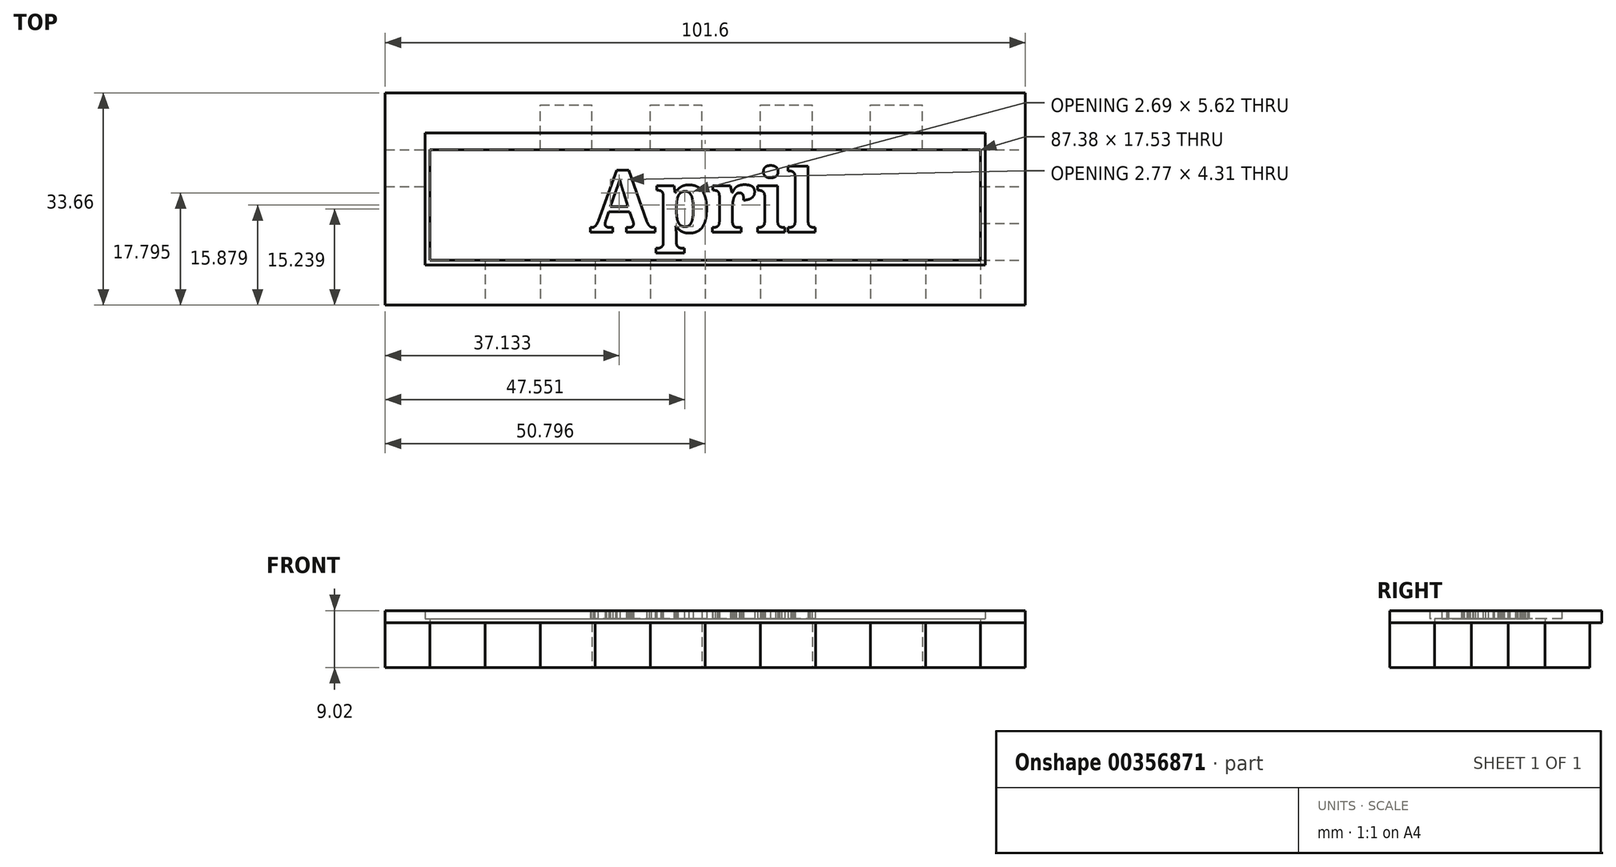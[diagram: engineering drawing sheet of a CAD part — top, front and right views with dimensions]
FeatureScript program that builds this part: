
annotation { "Feature Type Name" : "Feature", "Feature Type Description" : "" }
export const myFeature = defineFeature(function(context is Context, id is Id, definition is map)
    precondition{}
    {
        {
            var Q0;
            Q0=qCreatedBy(makeId("Top.planeOp"),FACE);
            var sketch = newSketch(context, id + "F0", { "sketchPlane" : qUnion([Q0])});
            skLineSegment(sketch, "E0.bottom", {"start": v(-52.12, 11.37) * mm, "end": v(49.48, 11.37) * mm});
            skLineSegment(sketch, "E0.top", {"start": v(-52.12, -20.38) * mm, "end": v(49.48, -20.38) * mm});
            skLineSegment(sketch, "E0.left", {"start": v(-52.12, 11.37) * mm, "end": v(-52.12, -20.38) * mm});
            skLineSegment(sketch, "E0.right", {"start": v(49.48, 11.37) * mm, "end": v(49.48, -20.38) * mm});
            skLineSegment(sketch, "E1.bottom", {"start": v(-52.12, 11.37) * mm, "end": v(-45.01, 11.37) * mm});
            skLineSegment(sketch, "E1.top", {"start": v(-52.12, 4.26) * mm, "end": v(-45.01, 4.26) * mm});
            skLineSegment(sketch, "E1.left", {"start": v(-52.12, 11.37) * mm, "end": v(-52.12, 4.26) * mm});
            skLineSegment(sketch, "E1.right", {"start": v(-45.01, 11.37) * mm, "end": v(-45.01, 4.26) * mm});
            skLineSegment(sketch, "E2.bottom", {"start": v(-45.01, 11.37) * mm, "end": v(-36.78, 11.37) * mm});
            skLineSegment(sketch, "E2.top", {"start": v(-45.01, 4.26) * mm, "end": v(-36.78, 4.26) * mm});
            skLineSegment(sketch, "E2.right", {"start": v(-36.78, 11.37) * mm, "end": v(-36.78, 4.26) * mm});
            skLineSegment(sketch, "E3.bottom", {"start": v(-36.78, 4.26) * mm, "end": v(-27.54, 4.26) * mm});
            skLineSegment(sketch, "E3.top", {"start": v(-36.78, 11.37) * mm, "end": v(-27.54, 11.37) * mm});
            skLineSegment(sketch, "E3.left", {"start": v(-36.78, 4.26) * mm, "end": v(-36.78, 11.37) * mm});
            skLineSegment(sketch, "E3.right", {"start": v(-27.54, 4.26) * mm, "end": v(-27.54, 11.37) * mm});
            skLineSegment(sketch, "E4.bottom", {"start": v(-27.54, 4.26) * mm, "end": v(-19.3, 4.26) * mm});
            skLineSegment(sketch, "E4.top", {"start": v(-27.54, 11.37) * mm, "end": v(-19.3, 11.37) * mm});
            skLineSegment(sketch, "E4.right", {"start": v(-19.3, 4.26) * mm, "end": v(-19.3, 11.37) * mm});
            skLineSegment(sketch, "E5.bottom", {"start": v(-19.3, 4.26) * mm, "end": v(-10.06, 4.26) * mm});
            skLineSegment(sketch, "E5.top", {"start": v(-19.3, 11.37) * mm, "end": v(-10.06, 11.37) * mm});
            skLineSegment(sketch, "E5.right", {"start": v(-10.06, 4.26) * mm, "end": v(-10.06, 11.37) * mm});
            skLineSegment(sketch, "E6.bottom", {"start": v(-10.06, 4.26) * mm, "end": v(-10.06, 4.26) * mm});
            skLineSegment(sketch, "E6.top", {"start": v(-10.06, 11.37) * mm, "end": v(-10.06, 11.37) * mm});
            skLineSegment(sketch, "E7.bottom", {"start": v(-10.06, 4.26) * mm, "end": v(-1.83, 4.26) * mm});
            skLineSegment(sketch, "E7.top", {"start": v(-10.06, 11.37) * mm, "end": v(-1.83, 11.37) * mm});
            skLineSegment(sketch, "E7.right", {"start": v(-1.83, 4.26) * mm, "end": v(-1.83, 11.37) * mm});
            skLineSegment(sketch, "E8.bottom", {"start": v(-1.83, 4.26) * mm, "end": v(7.41, 4.26) * mm});
            skLineSegment(sketch, "E8.top", {"start": v(-1.83, 11.37) * mm, "end": v(7.41, 11.37) * mm});
            skLineSegment(sketch, "E8.right", {"start": v(7.41, 4.26) * mm, "end": v(7.41, 11.37) * mm});
            skLineSegment(sketch, "E9.bottom", {"start": v(7.41, 4.26) * mm, "end": v(15.64, 4.26) * mm});
            skLineSegment(sketch, "E9.top", {"start": v(7.41, 11.37) * mm, "end": v(15.64, 11.37) * mm});
            skLineSegment(sketch, "E9.right", {"start": v(15.64, 4.26) * mm, "end": v(15.64, 11.37) * mm});
            skLineSegment(sketch, "E10.bottom", {"start": v(15.64, 4.26) * mm, "end": v(24.89, 4.26) * mm});
            skLineSegment(sketch, "E10.top", {"start": v(15.64, 11.37) * mm, "end": v(24.89, 11.37) * mm});
            skLineSegment(sketch, "E10.right", {"start": v(24.89, 4.26) * mm, "end": v(24.89, 11.37) * mm});
            skLineSegment(sketch, "E11.bottom", {"start": v(24.89, 4.26) * mm, "end": v(24.89, 4.26) * mm});
            skLineSegment(sketch, "E11.top", {"start": v(24.89, 11.37) * mm, "end": v(24.89, 11.37) * mm});
            skLineSegment(sketch, "E12.bottom", {"start": v(24.89, 4.26) * mm, "end": v(33.12, 4.26) * mm});
            skLineSegment(sketch, "E12.top", {"start": v(24.89, 11.37) * mm, "end": v(33.12, 11.37) * mm});
            skLineSegment(sketch, "E12.right", {"start": v(33.12, 4.26) * mm, "end": v(33.12, 11.37) * mm});
            skLineSegment(sketch, "E13.bottom", {"start": v(33.12, 4.26) * mm, "end": v(42.36, 4.26) * mm});
            skLineSegment(sketch, "E13.top", {"start": v(33.12, 11.37) * mm, "end": v(42.36, 11.37) * mm});
            skLineSegment(sketch, "E13.right", {"start": v(42.36, 4.26) * mm, "end": v(42.36, 11.37) * mm});
            skLineSegment(sketch, "E14.bottom", {"start": v(42.36, 4.26) * mm, "end": v(49.48, 4.26) * mm});
            skLineSegment(sketch, "E14.top", {"start": v(42.36, 11.37) * mm, "end": v(49.48, 11.37) * mm});
            skLineSegment(sketch, "E14.right", {"start": v(49.48, 4.26) * mm, "end": v(49.48, 11.37) * mm});
            skLineSegment(sketch, "E15.bottom", {"start": v(-52.12, -20.38) * mm, "end": v(-45.01, -20.38) * mm});
            skLineSegment(sketch, "E15.top", {"start": v(-52.12, -13.26) * mm, "end": v(-45.01, -13.26) * mm});
            skLineSegment(sketch, "E15.left", {"start": v(-52.12, -20.38) * mm, "end": v(-52.12, -13.26) * mm});
            skLineSegment(sketch, "E15.right", {"start": v(-45.01, -20.38) * mm, "end": v(-45.01, -13.26) * mm});
            skLineSegment(sketch, "E16.bottom", {"start": v(-45.01, -13.26) * mm, "end": v(-45.01, -13.26) * mm});
            skLineSegment(sketch, "E16.top", {"start": v(-45.01, -20.38) * mm, "end": v(-45.01, -20.38) * mm});
            skLineSegment(sketch, "E16.left", {"start": v(-45.01, -13.26) * mm, "end": v(-45.01, -20.38) * mm});
            skLineSegment(sketch, "E16.right", {"start": v(-45.01, -13.26) * mm, "end": v(-45.01, -20.38) * mm});
            skLineSegment(sketch, "E17.bottom", {"start": v(-45.01, -13.26) * mm, "end": v(-36.27, -13.26) * mm});
            skLineSegment(sketch, "E17.top", {"start": v(-45.01, -20.38) * mm, "end": v(-36.27, -20.38) * mm});
            skLineSegment(sketch, "E17.right", {"start": v(-36.27, -13.26) * mm, "end": v(-36.27, -20.38) * mm});
            skLineSegment(sketch, "E18.bottom", {"start": v(-36.27, -13.26) * mm, "end": v(-36.27, -13.26) * mm});
            skLineSegment(sketch, "E18.top", {"start": v(-36.27, -20.38) * mm, "end": v(-36.27, -20.38) * mm});
            skLineSegment(sketch, "E19.bottom", {"start": v(-36.27, -13.26) * mm, "end": v(-27.54, -13.26) * mm});
            skLineSegment(sketch, "E19.top", {"start": v(-36.27, -20.38) * mm, "end": v(-27.54, -20.38) * mm});
            skLineSegment(sketch, "E19.right", {"start": v(-27.54, -13.26) * mm, "end": v(-27.54, -20.38) * mm});
            skLineSegment(sketch, "E20.bottom", {"start": v(-27.54, -13.26) * mm, "end": v(-18.8, -13.26) * mm});
            skLineSegment(sketch, "E20.top", {"start": v(-27.54, -20.38) * mm, "end": v(-18.8, -20.38) * mm});
            skLineSegment(sketch, "E20.right", {"start": v(-18.8, -13.26) * mm, "end": v(-18.8, -20.38) * mm});
            skLineSegment(sketch, "E21.bottom", {"start": v(-18.8, -13.26) * mm, "end": v(-10.06, -13.26) * mm});
            skLineSegment(sketch, "E21.top", {"start": v(-18.8, -20.38) * mm, "end": v(-10.06, -20.38) * mm});
            skLineSegment(sketch, "E21.right", {"start": v(-10.06, -13.26) * mm, "end": v(-10.06, -20.38) * mm});
            skLineSegment(sketch, "E22.bottom", {"start": v(-10.06, -13.26) * mm, "end": v(-1.32, -13.26) * mm});
            skLineSegment(sketch, "E22.top", {"start": v(-10.06, -20.38) * mm, "end": v(-1.32, -20.38) * mm});
            skLineSegment(sketch, "E22.right", {"start": v(-1.32, -13.26) * mm, "end": v(-1.32, -20.38) * mm});
            skLineSegment(sketch, "E23.bottom", {"start": v(-1.32, -13.26) * mm, "end": v(7.41, -13.26) * mm});
            skLineSegment(sketch, "E23.top", {"start": v(-1.32, -20.38) * mm, "end": v(7.41, -20.38) * mm});
            skLineSegment(sketch, "E23.right", {"start": v(7.41, -13.26) * mm, "end": v(7.41, -20.38) * mm});
            skLineSegment(sketch, "E24.bottom", {"start": v(7.41, -13.26) * mm, "end": v(16.15, -13.26) * mm});
            skLineSegment(sketch, "E24.top", {"start": v(7.41, -20.38) * mm, "end": v(16.15, -20.38) * mm});
            skLineSegment(sketch, "E24.right", {"start": v(16.15, -13.26) * mm, "end": v(16.15, -20.38) * mm});
            skLineSegment(sketch, "E25.bottom", {"start": v(16.15, -13.26) * mm, "end": v(24.89, -13.26) * mm});
            skLineSegment(sketch, "E25.top", {"start": v(16.15, -20.38) * mm, "end": v(24.89, -20.38) * mm});
            skLineSegment(sketch, "E25.right", {"start": v(24.89, -13.26) * mm, "end": v(24.89, -20.38) * mm});
            skLineSegment(sketch, "E26.bottom", {"start": v(24.89, -13.26) * mm, "end": v(33.63, -13.26) * mm});
            skLineSegment(sketch, "E26.top", {"start": v(24.89, -20.38) * mm, "end": v(33.63, -20.38) * mm});
            skLineSegment(sketch, "E26.right", {"start": v(33.63, -13.26) * mm, "end": v(33.63, -20.38) * mm});
            skLineSegment(sketch, "E27.bottom", {"start": v(33.63, -13.26) * mm, "end": v(42.36, -13.26) * mm});
            skLineSegment(sketch, "E27.top", {"start": v(33.63, -20.38) * mm, "end": v(42.36, -20.38) * mm});
            skLineSegment(sketch, "E27.right", {"start": v(42.36, -13.26) * mm, "end": v(42.36, -20.38) * mm});
            skLineSegment(sketch, "E28.bottom", {"start": v(42.36, -13.26) * mm, "end": v(49.48, -13.26) * mm});
            skLineSegment(sketch, "E28.top", {"start": v(42.36, -20.38) * mm, "end": v(49.48, -20.38) * mm});
            skLineSegment(sketch, "E28.right", {"start": v(49.48, -13.26) * mm, "end": v(49.48, -20.38) * mm});
            skLineSegment(sketch, "E29.top", {"start": v(-52.12, -1.58) * mm, "end": v(-45.01, -1.58) * mm});
            skLineSegment(sketch, "E29.left", {"start": v(-52.12, 4.26) * mm, "end": v(-52.12, -1.58) * mm});
            skLineSegment(sketch, "E29.right", {"start": v(-45.01, 4.26) * mm, "end": v(-45.01, -1.58) * mm});
            skLineSegment(sketch, "E30.top", {"start": v(-52.12, -7.42) * mm, "end": v(-45.01, -7.42) * mm});
            skLineSegment(sketch, "E30.left", {"start": v(-52.12, -1.58) * mm, "end": v(-52.12, -7.42) * mm});
            skLineSegment(sketch, "E30.right", {"start": v(-45.01, -1.58) * mm, "end": v(-45.01, -7.42) * mm});
            skLineSegment(sketch, "E31.bottom", {"start": v(-45.01, -7.42) * mm, "end": v(-52.12, -7.42) * mm});
            skLineSegment(sketch, "E31.top", {"start": v(-45.01, -13.26) * mm, "end": v(-52.12, -13.26) * mm});
            skLineSegment(sketch, "E31.left", {"start": v(-45.01, -7.42) * mm, "end": v(-45.01, -13.26) * mm});
            skLineSegment(sketch, "E31.right", {"start": v(-52.12, -7.42) * mm, "end": v(-52.12, -13.26) * mm});
            skLineSegment(sketch, "E32.top", {"start": v(42.36, -1.58) * mm, "end": v(49.48, -1.58) * mm});
            skLineSegment(sketch, "E32.left", {"start": v(42.36, 4.26) * mm, "end": v(42.36, -1.58) * mm});
            skLineSegment(sketch, "E32.right", {"start": v(49.48, 4.26) * mm, "end": v(49.48, -1.58) * mm});
            skLineSegment(sketch, "E33.top", {"start": v(42.36, -7.42) * mm, "end": v(49.48, -7.42) * mm});
            skLineSegment(sketch, "E33.left", {"start": v(42.36, -1.58) * mm, "end": v(42.36, -7.42) * mm});
            skLineSegment(sketch, "E33.right", {"start": v(49.48, -1.58) * mm, "end": v(49.48, -7.42) * mm});
            skLineSegment(sketch, "E34.left", {"start": v(42.36, -7.42) * mm, "end": v(42.36, -13.26) * mm});
            skLineSegment(sketch, "E34.right", {"start": v(49.48, -7.42) * mm, "end": v(49.48, -13.26) * mm});
            skSolve(sketch);
        }
        {
            var Q0;
            Q0=makeQuery(id+"F0.imprint","IMPRINT",FACE,{"disambiguationData":[TD([[makeQuery(id+"F0.imprint","IMPRINT",EDGE,{"derivedFrom":sQuery(id+"F0.wireOp",EDGE,"E2.top")}),-1.0]])]});
            var Q1;
            Q1=makeQuery(id+"F0.imprint","IMPRINT",FACE,{"disambiguationData":[TD([[makeQuery(id+"F0.imprint","IMPRINT",EDGE,{"derivedFrom":sQuery(id+"F0.wireOp",EDGE,"E2.bottom")}),-1.0]])]});
            var Q2;
            Q2=makeQuery(id+"F0.imprint","IMPRINT",FACE,{"disambiguationData":[TD([[makeQuery(id+"F0.imprint","IMPRINT",EDGE,{"derivedFrom":sQuery(id+"F0.wireOp",EDGE,"E4.bottom")}),1.0]])]});
            var Q3;
            Q3=makeQuery(id+"F0.imprint","IMPRINT",FACE,{"disambiguationData":[TD([[makeQuery(id+"F0.imprint","IMPRINT",EDGE,{"derivedFrom":sQuery(id+"F0.wireOp",EDGE,"E7.bottom")}),1.0]])]});
            var Q4;
            Q4=makeQuery(id+"F0.imprint","IMPRINT",FACE,{"disambiguationData":[TD([[makeQuery(id+"F0.imprint","IMPRINT",EDGE,{"derivedFrom":sQuery(id+"F0.wireOp",EDGE,"E9.bottom")}),1.0]])]});
            var Q5;
            Q5=makeQuery(id+"F0.imprint","IMPRINT",FACE,{"disambiguationData":[TD([[makeQuery(id+"F0.imprint","IMPRINT",EDGE,{"derivedFrom":sQuery(id+"F0.wireOp",EDGE,"E12.bottom")}),1.0]])]});
            var Q6;
            Q6=makeQuery(id+"F0.imprint","IMPRINT",FACE,{"disambiguationData":[TD([[makeQuery(id+"F0.imprint","IMPRINT",EDGE,{"derivedFrom":sQuery(id+"F0.wireOp",EDGE,"E14.bottom")}),-1.0]])]});
            var Q7;
            Q7=makeQuery(id+"F0.imprint","IMPRINT",FACE,{"disambiguationData":[TD([[makeQuery(id+"F0.imprint","IMPRINT",EDGE,{"derivedFrom":sQuery(id+"F0.wireOp",EDGE,"E33.top")}),-1.0]])]});
            var Q8;
            Q8=makeQuery(id+"F0.imprint","IMPRINT",FACE,{"disambiguationData":[TD([[makeQuery(id+"F0.imprint","IMPRINT",EDGE,{"derivedFrom":sQuery(id+"F0.wireOp",EDGE,"E27.bottom")}),-1.0]])]});
            var Q9;
            Q9=makeQuery(id+"F0.imprint","IMPRINT",FACE,{"disambiguationData":[TD([[makeQuery(id+"F0.imprint","IMPRINT",EDGE,{"derivedFrom":sQuery(id+"F0.wireOp",EDGE,"E25.bottom")}),-1.0]])]});
            var Q10;
            Q10=makeQuery(id+"F0.imprint","IMPRINT",FACE,{"disambiguationData":[TD([[makeQuery(id+"F0.imprint","IMPRINT",EDGE,{"derivedFrom":sQuery(id+"F0.wireOp",EDGE,"E23.bottom")}),-1.0]])]});
            var Q11;
            Q11=makeQuery(id+"F0.imprint","IMPRINT",FACE,{"disambiguationData":[TD([[makeQuery(id+"F0.imprint","IMPRINT",EDGE,{"derivedFrom":sQuery(id+"F0.wireOp",EDGE,"E21.bottom")}),-1.0]])]});
            var Q12;
            Q12=makeQuery(id+"F0.imprint","IMPRINT",FACE,{"disambiguationData":[TD([[makeQuery(id+"F0.imprint","IMPRINT",EDGE,{"derivedFrom":sQuery(id+"F0.wireOp",EDGE,"E19.bottom")}),-1.0]])]});
            var Q13;
            Q13=makeQuery(id+"F0.imprint","IMPRINT",FACE,{"disambiguationData":[TD([[makeQuery(id+"F0.imprint","IMPRINT",EDGE,{"derivedFrom":sQuery(id+"F0.wireOp",EDGE,"E31.bottom")}),1.0]])]});
            var Q14;
            Q14=makeQuery(id+"F0.imprint","IMPRINT",FACE,{"disambiguationData":[TD([[makeQuery(id+"F0.imprint","IMPRINT",EDGE,{"derivedFrom":sQuery(id+"F0.wireOp",EDGE,"E1.top")}),-1.0]])]});
            extrude(context, id + "F1", {"entities" : qUnion([Q0, Q1, Q2, Q3, Q4, Q5, Q6, Q7, Q8, Q9, Q10, Q11, Q12, Q13, Q14]), "depth" : 7.11 * mm});
        }
        {
            var Q0;
            Q0=makeQuery(id+"F1.opExtrude","CAP_FACE",FACE,{"disambiguationData":[OSD([sQuery(id+"F0.wireOp",EDGE,"E2.bottom"),sQuery(id+"F0.wireOp",EDGE,"E1.right"),sQuery(id+"F0.wireOp",EDGE,"E3.bottom"),sQuery(id+"F0.wireOp",EDGE,"E3.left"),sQuery(id+"F0.wireOp",EDGE,"E4.top"),sQuery(id+"F0.wireOp",EDGE,"E3.right"),sQuery(id+"F0.wireOp",EDGE,"E5.bottom"),sQuery(id+"F0.wireOp",EDGE,"E4.right"),sQuery(id+"F0.wireOp",EDGE,"E6.top"),sQuery(id+"F0.wireOp",EDGE,"E5.right"),sQuery(id+"F0.wireOp",EDGE,"E7.bottom"),sQuery(id+"F0.wireOp",EDGE,"E5.right"),sQuery(id+"F0.wireOp",EDGE,"E8.top"),sQuery(id+"F0.wireOp",EDGE,"E7.right"),sQuery(id+"F0.wireOp",EDGE,"E9.bottom"),sQuery(id+"F0.wireOp",EDGE,"E8.right"),sQuery(id+"F0.wireOp",EDGE,"E10.top"),sQuery(id+"F0.wireOp",EDGE,"E9.right"),sQuery(id+"F0.wireOp",EDGE,"E11.bottom"),sQuery(id+"F0.wireOp",EDGE,"E10.right"),sQuery(id+"F0.wireOp",EDGE,"E12.top"),sQuery(id+"F0.wireOp",EDGE,"E10.right"),sQuery(id+"F0.wireOp",EDGE,"E13.bottom"),sQuery(id+"F0.wireOp",EDGE,"E12.right"),sQuery(id+"F0.wireOp",EDGE,"E16.bottom"),sQuery(id+"F0.wireOp",EDGE,"E17.top"),sQuery(id+"F0.wireOp",EDGE,"E16.left"),sQuery(id+"F0.wireOp",EDGE,"E18.bottom"),sQuery(id+"F0.wireOp",EDGE,"E17.right"),sQuery(id+"F0.wireOp",EDGE,"E19.top"),sQuery(id+"F0.wireOp",EDGE,"E17.right"),sQuery(id+"F0.wireOp",EDGE,"E20.bottom"),sQuery(id+"F0.wireOp",EDGE,"E19.right"),sQuery(id+"F0.wireOp",EDGE,"E21.top"),sQuery(id+"F0.wireOp",EDGE,"E20.right"),sQuery(id+"F0.wireOp",EDGE,"E22.bottom"),sQuery(id+"F0.wireOp",EDGE,"E21.right"),sQuery(id+"F0.wireOp",EDGE,"E23.top"),sQuery(id+"F0.wireOp",EDGE,"E22.right"),sQuery(id+"F0.wireOp",EDGE,"E24.bottom"),sQuery(id+"F0.wireOp",EDGE,"E23.right"),sQuery(id+"F0.wireOp",EDGE,"E25.top"),sQuery(id+"F0.wireOp",EDGE,"E24.right"),sQuery(id+"F0.wireOp",EDGE,"E26.bottom"),sQuery(id+"F0.wireOp",EDGE,"E25.right"),sQuery(id+"F0.wireOp",EDGE,"E27.top"),sQuery(id+"F0.wireOp",EDGE,"E26.right"),sQuery(id+"F0.wireOp",EDGE,"E27.right"),sQuery(id+"F0.wireOp",EDGE,"E1.top"),sQuery(id+"F0.wireOp",EDGE,"E29.left"),sQuery(id+"F0.wireOp",EDGE,"E29.top"),sQuery(id+"F0.wireOp",EDGE,"E30.right"),sQuery(id+"F0.wireOp",EDGE,"E31.bottom"),sQuery(id+"F0.wireOp",EDGE,"E31.top"),sQuery(id+"F0.wireOp",EDGE,"E31.right"),sQuery(id+"F0.wireOp",EDGE,"E14.bottom"),sQuery(id+"F0.wireOp",EDGE,"E32.right"),sQuery(id+"F0.wireOp",EDGE,"E32.top"),sQuery(id+"F0.wireOp",EDGE,"E33.left"),sQuery(id+"F0.wireOp",EDGE,"E33.top"),sQuery(id+"F0.wireOp",EDGE,"E28.bottom"),sQuery(id+"F0.wireOp",EDGE,"E34.right")])],"isStart":false});
            var sketch = newSketch(context, id + "F2", { "sketchPlane" : qUnion([Q0])});
            skLineSegment(sketch, "E35.bottom", {"start": v(-52.12, -20.38) * mm, "end": v(-45.01, -20.38) * mm});
            skLineSegment(sketch, "E35.top", {"start": v(-52.12, 13.28) * mm, "end": v(-45.01, 13.28) * mm});
            skLineSegment(sketch, "E35.left", {"start": v(-52.12, -20.38) * mm, "end": v(-52.12, 13.28) * mm});
            skLineSegment(sketch, "E35.right", {"start": v(-45.01, -20.38) * mm, "end": v(-45.01, 13.28) * mm});
            skLineSegment(sketch, "E36.bottom", {"start": v(-52.12, -20.38) * mm, "end": v(49.48, -20.38) * mm});
            skLineSegment(sketch, "E36.top", {"start": v(-52.12, -13.26) * mm, "end": v(49.48, -13.26) * mm});
            skLineSegment(sketch, "E36.left", {"start": v(-52.12, -20.38) * mm, "end": v(-52.12, -13.26) * mm});
            skLineSegment(sketch, "E36.right", {"start": v(49.48, -20.38) * mm, "end": v(49.48, -13.26) * mm});
            skPoint(sketch, "E37.oppositeSnap0", {"position": v(42.36, -4.5) * mm});
            skLineSegment(sketch, "E37.bottom", {"start": v(49.48, -20.38) * mm, "end": v(42.36, -20.38) * mm});
            skLineSegment(sketch, "E37.top", {"start": v(49.48, 13.28) * mm, "end": v(42.36, 13.28) * mm});
            skLineSegment(sketch, "E37.left", {"start": v(49.48, -20.38) * mm, "end": v(49.48, 13.28) * mm});
            skLineSegment(sketch, "E37.right", {"start": v(42.36, -20.38) * mm, "end": v(42.36, 13.28) * mm});
            skLineSegment(sketch, "E38.bottom", {"start": v(-52.12, 13.28) * mm, "end": v(49.48, 13.28) * mm});
            skLineSegment(sketch, "E38.top", {"start": v(-52.12, 4.26) * mm, "end": v(49.48, 4.26) * mm});
            skLineSegment(sketch, "E38.left", {"start": v(-52.12, 13.28) * mm, "end": v(-52.12, 4.26) * mm});
            skLineSegment(sketch, "E38.right", {"start": v(49.48, 13.28) * mm, "end": v(49.48, 4.26) * mm});
            skSolve(sketch);
        }
        {
            var Q0;
            Q0=qSketchRegion(id+"F2",true);
            var Q1;
            {var subQ5=sQuery(id+"F2.wireOp",EDGE,"E36.top");var subQ10=sQuery(id+"F2.wireOp",EDGE,"E35.right");var subQ12=makeQuery(id+"F2.imprint","INTERSECT",VERTEX,{"derivedFrom":[makeQuery(id+"F1.opExtrude","CAP_EDGE",EDGE,{"disambiguationData":[OSD([sQuery(id+"F0.wireOp",EDGE,"E31.bottom")])],"isStart":false}),subQ10]});var subQ24=makeQuery(id+"F2.imprint","INTERSECT",VERTEX,{"derivedFrom":[subQ10,subQ5]});Q1=makeQuery(id+"F2.imprint","IMPRINT",FACE,{"disambiguationData":[TD([[makeQuery(id+"F2.imprint","IMPRINT",EDGE,{"disambiguationData":[TD([[subQ12,1.0],[subQ24,-1.0]])],"derivedFrom":subQ10}),-1.0]])]});}
            extrude(context, id + "F3", {"entities" : qUnion([Q0, Q1]), "depth" : 0.64 * mm});
        }
        {
            var Q0;
            Q0=makeQuery(id+"F3.opExtrude","CAP_FACE",FACE,{"disambiguationData":[OSD([sQuery(id+"F2.wireOp",EDGE,"E35.left"),sQuery(id+"F2.wireOp",EDGE,"E36.bottom"),sQuery(id+"F2.wireOp",EDGE,"E36.left"),sQuery(id+"F2.wireOp",EDGE,"E37.bottom"),sQuery(id+"F2.wireOp",EDGE,"E37.left"),sQuery(id+"F2.wireOp",EDGE,"E38.bottom"),sQuery(id+"F2.wireOp",EDGE,"E38.left"),sQuery(id+"F2.wireOp",EDGE,"E38.right")])],"isStart":false});
            var sketch = newSketch(context, id + "F4", { "sketchPlane" : qUnion([Q0])});
            skLineSegment(sketch, "E39.bottom", {"start": v(-52.12, 13.28) * mm, "end": v(49.48, 13.28) * mm});
            skLineSegment(sketch, "E39.top", {"start": v(-52.12, 6.93) * mm, "end": v(49.48, 6.93) * mm});
            skLineSegment(sketch, "E39.left", {"start": v(-52.12, 13.28) * mm, "end": v(-52.12, 6.93) * mm});
            skLineSegment(sketch, "E39.right", {"start": v(49.48, 13.28) * mm, "end": v(49.48, 6.93) * mm});
            skLineSegment(sketch, "E40.bottom", {"start": v(-52.12, 13.28) * mm, "end": v(-45.77, 13.28) * mm});
            skLineSegment(sketch, "E40.top", {"start": v(-52.12, -20.38) * mm, "end": v(-45.77, -20.38) * mm});
            skLineSegment(sketch, "E40.left", {"start": v(-52.12, 13.28) * mm, "end": v(-52.12, -20.38) * mm});
            skLineSegment(sketch, "E40.right", {"start": v(-45.77, 13.28) * mm, "end": v(-45.77, -20.38) * mm});
            skLineSegment(sketch, "E41.bottom", {"start": v(-52.12, -14.03) * mm, "end": v(49.48, -14.03) * mm});
            skLineSegment(sketch, "E41.top", {"start": v(-52.12, -20.38) * mm, "end": v(49.48, -20.38) * mm});
            skLineSegment(sketch, "E41.left", {"start": v(-52.12, -14.03) * mm, "end": v(-52.12, -20.38) * mm});
            skLineSegment(sketch, "E41.right", {"start": v(49.48, -14.03) * mm, "end": v(49.48, -20.38) * mm});
            skLineSegment(sketch, "E42.bottom", {"start": v(49.48, -20.38) * mm, "end": v(43.13, -20.38) * mm});
            skLineSegment(sketch, "E42.top", {"start": v(49.48, 13.28) * mm, "end": v(43.13, 13.28) * mm});
            skLineSegment(sketch, "E42.left", {"start": v(49.48, -20.38) * mm, "end": v(49.48, 13.28) * mm});
            skLineSegment(sketch, "E42.right", {"start": v(43.13, -20.38) * mm, "end": v(43.13, 13.28) * mm});
            skSolve(sketch);
        }
        {
            var Q0;
            Q0=qSketchRegion(id+"F4",true);
            extrude(context, id + "F5", {"entities" : qUnion([Q0]), "operationType" : NewBodyOperationType.ADD, "depth" : 1.27 * mm});
        }
        {
            var Q0;
            Q0=makeQuery(id+"F3.opExtrude","CAP_FACE",FACE,{"disambiguationData":[OSD([sQuery(id+"F2.wireOp",EDGE,"E35.left"),sQuery(id+"F2.wireOp",EDGE,"E36.bottom"),sQuery(id+"F2.wireOp",EDGE,"E36.left"),sQuery(id+"F2.wireOp",EDGE,"E37.bottom"),sQuery(id+"F2.wireOp",EDGE,"E37.left"),sQuery(id+"F2.wireOp",EDGE,"E38.bottom"),sQuery(id+"F2.wireOp",EDGE,"E38.left"),sQuery(id+"F2.wireOp",EDGE,"E38.right")])],"isStart":false});
            var sketch = newSketch(context, id + "F6", { "sketchPlane" : qUnion([Q0])});
            skText(sketch, "E43", { "text": "April", "fontName": "NotoSerif-Bold.ttf"});
            const initialGuessF6  = {"E43": [-0.01965, -0.0088, 1, 0, 0.00988]};
            skSetInitialGuess(sketch, initialGuessF6);
            skSolve(sketch);
        }
        {
            var Q0;
            Q0 = qSketchRegion(id + "F6", true);
            extrude(context, id + "F7", {"entities" : qUnion([Q0]), "operationType" : NewBodyOperationType.ADD, "depth" : 1.27 * mm});
        }
    });
